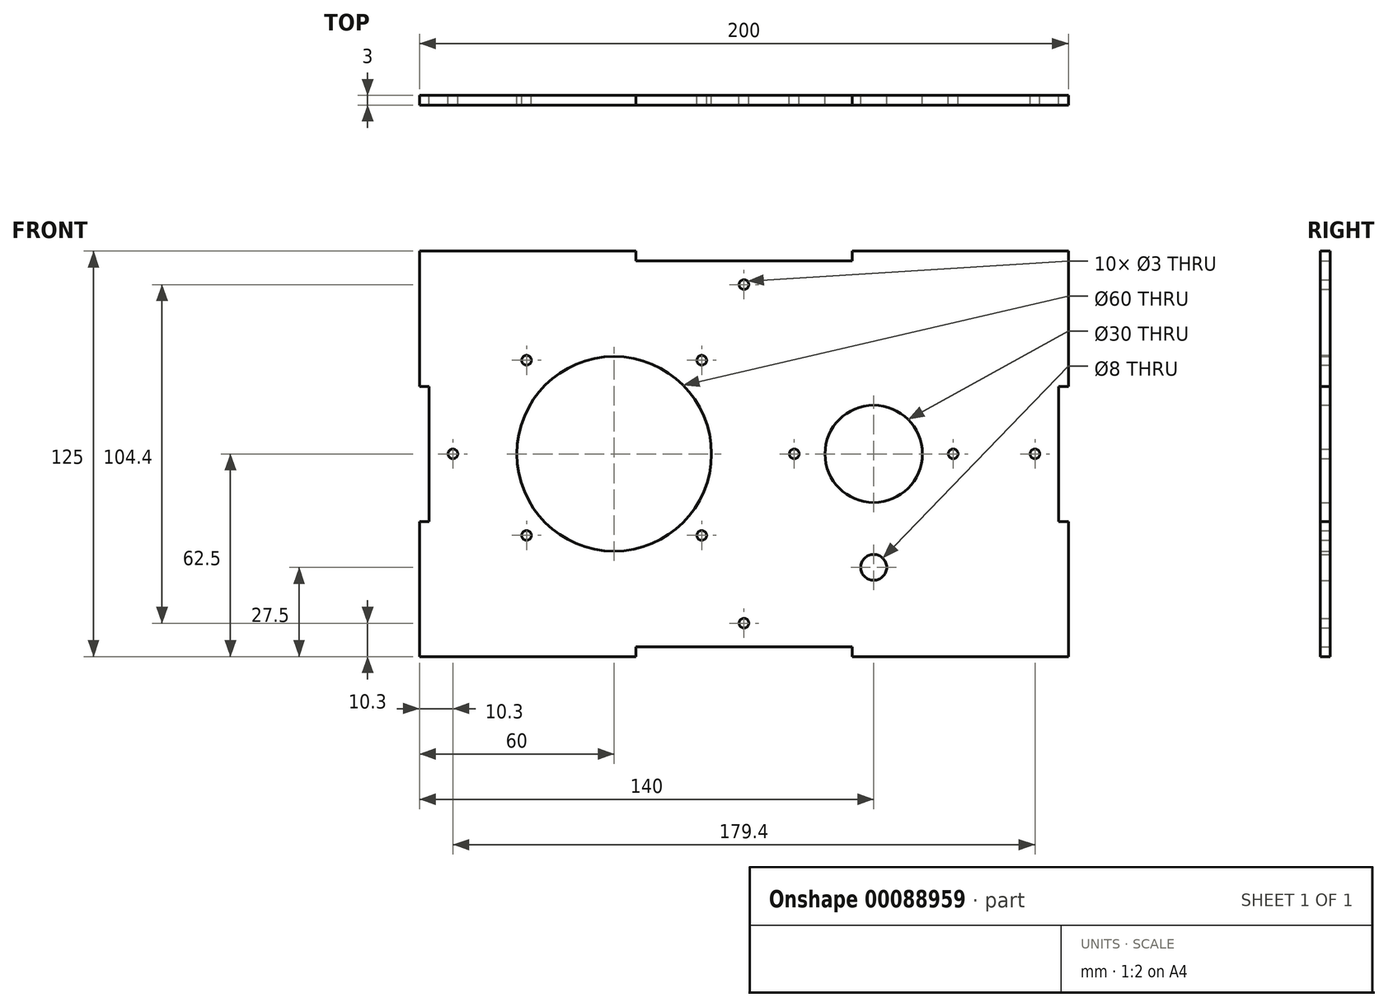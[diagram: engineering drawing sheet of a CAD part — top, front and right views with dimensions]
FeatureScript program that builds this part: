
annotation { "Feature Type Name" : "Feature", "Feature Type Description" : "" }
export const myFeature = defineFeature(function(context is Context, id is Id, definition is map)
    precondition{}
    {
        {
            var Q0;
            Q0=qCreatedBy(makeId("Front.planeOp"),FACE);
            var sketch = newSketch(context, id + "F0", { "sketchPlane" : qUnion([Q0])});
            skLineSegment(sketch, "E0.top", {"start": v(-100, -62.5) * mm, "end": v(-33.33, -62.5) * mm});
            skLineSegment(sketch, "E0.left", {"start": v(-100, 62.5) * mm, "end": v(-100, 20.83) * mm});
            skLineSegment(sketch, "E0.right", {"start": v(100, 62.5) * mm, "end": v(100, 20.83) * mm});
            skPoint(sketch, "E0.middle", {"position": v(0, 0) * mm});
            skLineSegment(sketch, "E1", {"start": v(-100, 62.5) * mm, "end": v(-33.33, 62.5) * mm});
            skLineSegment(sketch, "E2", {"start": v(-33.33, 62.5) * mm, "end": v(-33.33, 59.5) * mm});
            skLineSegment(sketch, "E3", {"start": v(-33.33, 59.5) * mm, "end": v(33.33, 59.5) * mm});
            skLineSegment(sketch, "E4", {"start": v(33.33, 59.5) * mm, "end": v(33.33, 62.5) * mm});
            skLineSegment(sketch, "E5", {"start": v(33.33, 62.5) * mm, "end": v(100, 62.5) * mm});
            skLineSegment(sketch, "E6", {"start": v(100, 20.83) * mm, "end": v(97, 20.83) * mm});
            skLineSegment(sketch, "E7", {"start": v(97, 20.83) * mm, "end": v(97, -20.83) * mm});
            skLineSegment(sketch, "E8", {"start": v(97, -20.83) * mm, "end": v(100, -20.83) * mm});
            skLineSegment(sketch, "E9.trimOffspring", {"start": v(100, -20.83) * mm, "end": v(100, -62.5) * mm});
            skLineSegment(sketch, "E10", {"start": v(-100, 20.83) * mm, "end": v(-97, 20.83) * mm});
            skLineSegment(sketch, "E11", {"start": v(-97, 20.83) * mm, "end": v(-97, -20.83) * mm});
            skLineSegment(sketch, "E12", {"start": v(-97, -20.83) * mm, "end": v(-100, -20.83) * mm});
            skLineSegment(sketch, "E13", {"start": v(-33.33, -62.5) * mm, "end": v(-33.33, -59.5) * mm});
            skLineSegment(sketch, "E14", {"start": v(-33.33, -59.5) * mm, "end": v(33.33, -59.5) * mm});
            skLineSegment(sketch, "E15", {"start": v(33.33, -59.5) * mm, "end": v(33.33, -62.5) * mm});
            skLineSegment(sketch, "E16.trimOffspring", {"start": v(-100, -20.83) * mm, "end": v(-100, -62.5) * mm});
            skLineSegment(sketch, "E17.trimOffspring", {"start": v(33.33, -62.5) * mm, "end": v(100, -62.5) * mm});
            skCircle(sketch, "E18", {"center": v(-40, 0) * mm, "radius": 30 * mm});
            skCircle(sketch, "E19", {"center": v(40, 0) * mm, "radius": 15 * mm});
            skCircle(sketch, "E20", {"center": v(15.5, 0) * mm, "radius": 1.5 * mm});
            skCircle(sketch, "E21", {"center": v(64.5, 0) * mm, "radius": 1.5 * mm});
            skLineSegment(sketch, "E22", {"start": v(40, 9.89) * mm, "end": v(40, -7.64) * mm, "construction": true});
            skLineSegment(sketch, "E23", {"start": v(-40, 19.35) * mm, "end": v(-40, -22.88) * mm, "construction": true});
            skCircle(sketch, "E24", {"center": v(-67, 28.87) * mm, "radius": 1.5 * mm});
            skCircle(sketch, "E25", {"center": v(-67, -25.13) * mm, "radius": 1.5 * mm});
            skCircle(sketch, "E26", {"center": v(-13, -25.13) * mm, "radius": 1.5 * mm});
            skCircle(sketch, "E27", {"center": v(-13, 28.87) * mm, "radius": 1.5 * mm});
            skCircle(sketch, "E28", {"center": v(40, -35) * mm, "radius": 4 * mm});
            skLineSegment(sketch, "E29.bottom", {"start": v(-67, 28.87) * mm, "end": v(-13, 28.87) * mm, "construction": true});
            skLineSegment(sketch, "E29.top", {"start": v(-67, -25.13) * mm, "end": v(-13, -25.13) * mm, "construction": true});
            skLineSegment(sketch, "E29.left", {"start": v(-67, 28.87) * mm, "end": v(-67, -25.13) * mm, "construction": true});
            skLineSegment(sketch, "E29.right", {"start": v(-13, 28.87) * mm, "end": v(-13, -25.13) * mm, "construction": true});
            skCircle(sketch, "E30", {"center": v(0, 52.2) * mm, "radius": 1.5 * mm});
            skCircle(sketch, "E31", {"center": v(89.7, 0) * mm, "radius": 1.5 * mm});
            skCircle(sketch, "E32", {"center": v(0, -52.2) * mm, "radius": 1.5 * mm});
            skCircle(sketch, "E33", {"center": v(-89.7, 0) * mm, "radius": 1.5 * mm});
            skSolve(sketch);
        }
        {
            var Q0;
            Q0 = qSketchRegion(id + "F0", true);
            extrude(context, id + "F1", {"entities" : qUnion([Q0]), "depth" : 3 * mm});
        }
        {
            var Q0;
            Q0=makeQuery(id+"F1.opExtrude","SWEPT_BODY",BODY,{"disambiguationData":[OSD([sQuery(id+"F0.wireOp",EDGE,"E0.top"),sQuery(id+"F0.wireOp",EDGE,"E0.left"),sQuery(id+"F0.wireOp",EDGE,"E0.right"),sQuery(id+"F0.wireOp",EDGE,"E1"),sQuery(id+"F0.wireOp",EDGE,"E2"),sQuery(id+"F0.wireOp",EDGE,"E3"),sQuery(id+"F0.wireOp",EDGE,"E4"),sQuery(id+"F0.wireOp",EDGE,"E5"),sQuery(id+"F0.wireOp",EDGE,"E6"),sQuery(id+"F0.wireOp",EDGE,"E7"),sQuery(id+"F0.wireOp",EDGE,"E8"),sQuery(id+"F0.wireOp",EDGE,"E9.trimOffspring"),sQuery(id+"F0.wireOp",EDGE,"E10"),sQuery(id+"F0.wireOp",EDGE,"E11"),sQuery(id+"F0.wireOp",EDGE,"E12"),sQuery(id+"F0.wireOp",EDGE,"E13"),sQuery(id+"F0.wireOp",EDGE,"E14"),sQuery(id+"F0.wireOp",EDGE,"E15"),sQuery(id+"F0.wireOp",EDGE,"E16.trimOffspring"),sQuery(id+"F0.wireOp",EDGE,"E17.trimOffspring"),sQuery(id+"F0.wireOp",EDGE,"E18"),sQuery(id+"F0.wireOp",EDGE,"E19"),sQuery(id+"F0.wireOp",EDGE,"E20"),sQuery(id+"F0.wireOp",EDGE,"E21"),sQuery(id+"F0.wireOp",EDGE,"E24"),sQuery(id+"F0.wireOp",EDGE,"E25"),sQuery(id+"F0.wireOp",EDGE,"E26"),sQuery(id+"F0.wireOp",EDGE,"E27"),sQuery(id+"F0.wireOp",EDGE,"E28"),sQuery(id+"F0.wireOp",EDGE,"E30"),sQuery(id+"F0.wireOp",EDGE,"E31"),sQuery(id+"F0.wireOp",EDGE,"E32"),sQuery(id+"F0.wireOp",EDGE,"E33")])]});
            transform(context, id + "F2", {"entities" : qUnion([Q0]), "transformType" : TransformType.TRANSLATION_3D, "dx" : 0 * mm, "dy" : 60 * mm, "dz" : 0 * mm, "makeCopy" : true});
        }
        {
            var Q0;
            Q0=makeQuery(id+"F2.opPattern","COPY",BODY,{"derivedFrom":makeQuery(id+"F1.opExtrude","SWEPT_BODY",BODY,{"disambiguationData":[OSD([sQuery(id+"F0.wireOp",EDGE,"E0.top"),sQuery(id+"F0.wireOp",EDGE,"E0.left"),sQuery(id+"F0.wireOp",EDGE,"E0.right"),sQuery(id+"F0.wireOp",EDGE,"E1"),sQuery(id+"F0.wireOp",EDGE,"E2"),sQuery(id+"F0.wireOp",EDGE,"E3"),sQuery(id+"F0.wireOp",EDGE,"E4"),sQuery(id+"F0.wireOp",EDGE,"E5"),sQuery(id+"F0.wireOp",EDGE,"E6"),sQuery(id+"F0.wireOp",EDGE,"E7"),sQuery(id+"F0.wireOp",EDGE,"E8"),sQuery(id+"F0.wireOp",EDGE,"E9.trimOffspring"),sQuery(id+"F0.wireOp",EDGE,"E10"),sQuery(id+"F0.wireOp",EDGE,"E11"),sQuery(id+"F0.wireOp",EDGE,"E12"),sQuery(id+"F0.wireOp",EDGE,"E13"),sQuery(id+"F0.wireOp",EDGE,"E14"),sQuery(id+"F0.wireOp",EDGE,"E15"),sQuery(id+"F0.wireOp",EDGE,"E16.trimOffspring"),sQuery(id+"F0.wireOp",EDGE,"E17.trimOffspring"),sQuery(id+"F0.wireOp",EDGE,"E18"),sQuery(id+"F0.wireOp",EDGE,"E19"),sQuery(id+"F0.wireOp",EDGE,"E20"),sQuery(id+"F0.wireOp",EDGE,"E21"),sQuery(id+"F0.wireOp",EDGE,"E24"),sQuery(id+"F0.wireOp",EDGE,"E25"),sQuery(id+"F0.wireOp",EDGE,"E26"),sQuery(id+"F0.wireOp",EDGE,"E27"),sQuery(id+"F0.wireOp",EDGE,"E28"),sQuery(id+"F0.wireOp",EDGE,"E30"),sQuery(id+"F0.wireOp",EDGE,"E31"),sQuery(id+"F0.wireOp",EDGE,"E32"),sQuery(id+"F0.wireOp",EDGE,"E33")])]}),"instanceName":"1"});
            deleteBodies(context, id + "F3", {"entities" : qUnion([Q0])});
        }
    });
